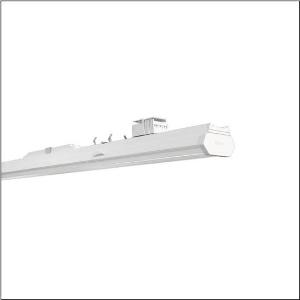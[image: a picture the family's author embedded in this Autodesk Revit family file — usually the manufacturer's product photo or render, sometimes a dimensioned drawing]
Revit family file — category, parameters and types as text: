
# Revit family: licross_21_protected_mo_52td11vn48xgd
name_source: partatom
category: Lighting Fixtures
units: mm (PartAtom-declared; Revit-internal decimal feet)

## family parameters
Cut with Voids When Loaded = No
Host = Face
Light Source = No
Part Type = Normal
Room Calculation Point = No
Round Connector Dimension = Use Diameter
Shared = No

## types (1)
- --- (1 x LED, 980 lm, 7 W, 4000K)
    Apparent Load = 7 VA
    CIE Flux Codes = 83 94 98 100 100
    Color Rendering = 80
    Color Temperature = 4000K
    Default Elevation = 1800 mm
    Description = Licross 21 Protected MO, luminaire insert, of sheet steel, galvanised, coil coated, white, length: 1.500mm, width: 90mm, height: 103mm, LED rated luminous flux: 8.000lm, light colour: 840, SDCM (Standard Deviation of Colour Matching)MacAdam ≤ 3 SDCM (initial), control gear: DALI 2, CLO (for two DALI lines), with plug, 6-pole, with phase selection, mains connection: 220..240V, AC/DC, 0/50..60Hz, start of lifetime: 46W, end of service life: 52W, without changeover relay, for emergency light function, for central battery installations according to EN 60598-2-22, internal wiring halogen-free, primary optical cover: cover, of PMMA, light emission: direct distribution, primary light characteristic: symmetric, protection rating (complete): IP54, insulation class (complete): insulation class I (protective earthing), certification: CE, ENEC, VDE, UKCA, protection symbol: D if used in an environment with non-conductive dust loads with corresponding accessories, impact resistance: IK06, permissible ambient temperature for indoor applications: -25..+50°C, standard: EN 60598-2-22, corresponds to IFS (International Featured Standards) requirements for safety and quality in the food industry, reducing of maximum allowable ambient temperature of 5°C with ceiling mounting, LABS conformity tested according to VDMA 24364:2018-05, The light source and the operating device comply with the requirements of the Ecodesign Regulation (EU) 2019/2020 and are replaceable in accordance with this regulation, packaging unit: 1 piece
    Height = 92 mm
    Lamp = 1 x LED
    Lamp Light Flux = 980 lm
    Lamp Power = 7 W
    Lamp count = 1
    Length = 1500 mm
    Luminous efficacy = 140 lm/W
    Manufacturer = Siteco
    ModVariant = No
    Model = 52TD11VN48XGD
    Mounting Place = Ceiling
    Mounting Type = Pendant
    Number of Poles = 1
    OnlyDefault = Yes
    Power Factor = 1
    Product Name = Licross 21 Protected MO
    Product group = luminaire insert | ceiling pendant
    ProductGroupID = 901
    Protection Class = Protection class I
    Protection Degree = IP 54
    RLX_Detail_Level = 1
    RLX_Emergency_Light_Flux = 0 lm
    RLX_Emergency_Type = 0
    RLX_Emergency_Type_DB = No
    RlxData = <blob elided: 24837 chars, md5=154b25e2>
    Socket = socket
    Standby Power = 0 W
    System Light Flux = 980 lm
    System Power = 7 W
    Type Comments = : DC mode (central or group accumulator) initial emergency light level
    Type Image = l_1256148.jpg
    URL = http://relux.com
    VarID = @adj_089215
    Voltage = 0 V
    Weight = 0.00 kg
    Width = 88 mm

## geometry (parser evidence)
native form markers: Blend x4, Sweep x12
no freeform markers — native parametric forms only
